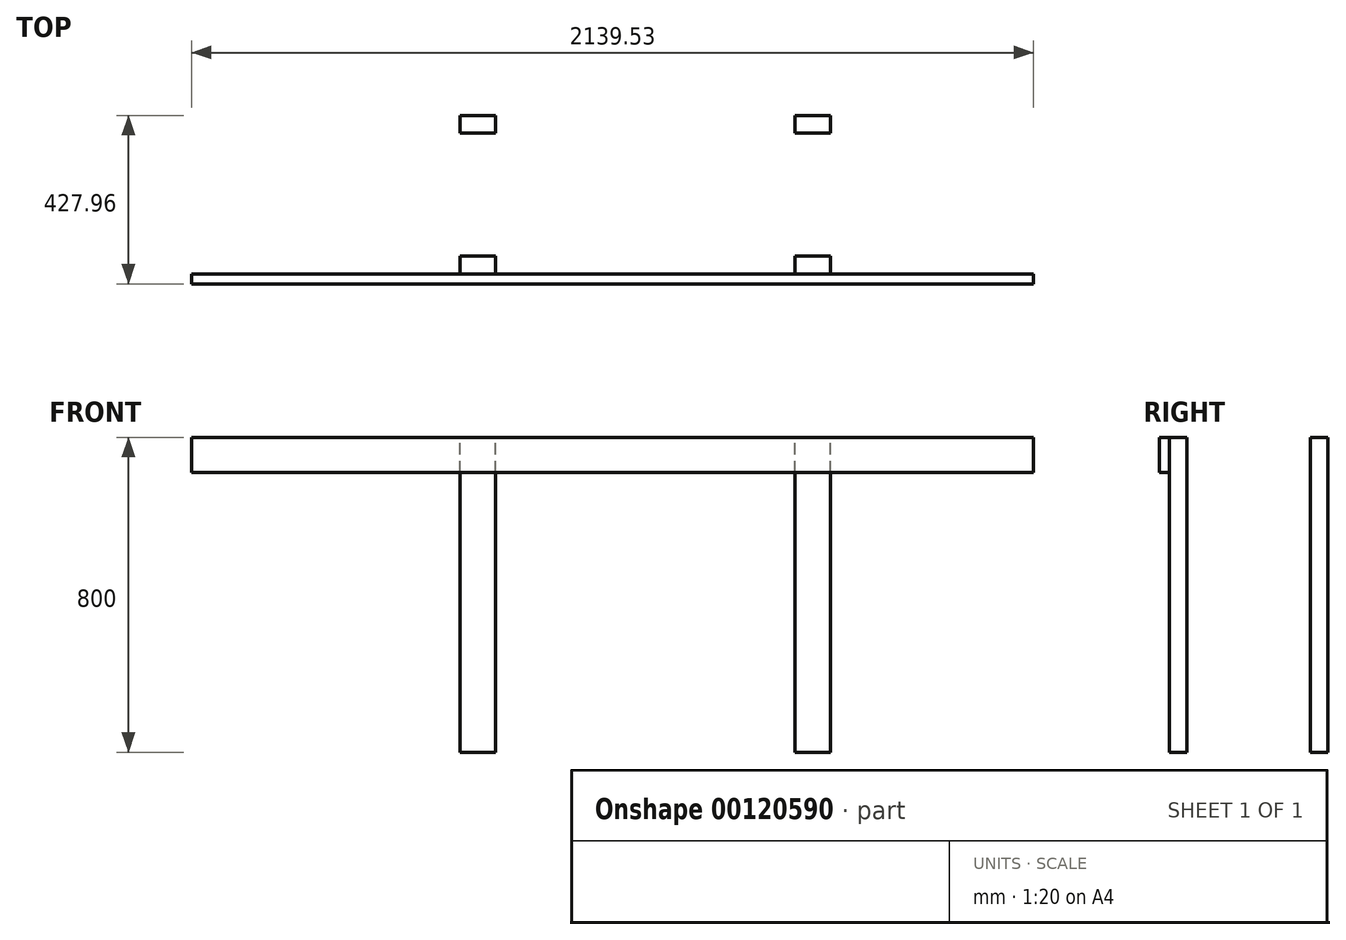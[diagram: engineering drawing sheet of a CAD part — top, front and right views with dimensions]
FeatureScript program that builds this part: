
annotation { "Feature Type Name" : "Feature", "Feature Type Description" : "" }
export const myFeature = defineFeature(function(context is Context, id is Id, definition is map)
    precondition{}
    {
        {
            var Q0;
            Q0=qCreatedBy(makeId("Top.planeOp"),FACE);
            var sketch = newSketch(context, id + "F0", { "sketchPlane" : qUnion([Q0])});
            skLineSegment(sketch, "E0", {"start": v(0, 886.7) * mm, "end": v(0, -768.07) * mm, "construction": true});
            skLineSegment(sketch, "E1", {"start": v(-826.36, 0) * mm, "end": v(826.36, 0) * mm, "construction": true});
            skLineSegment(sketch, "E2.bottom", {"start": v(-1200, 600) * mm, "end": v(1200, 600) * mm});
            skLineSegment(sketch, "E2.top", {"start": v(-1200, -600) * mm, "end": v(1200, -600) * mm});
            skLineSegment(sketch, "E2.left", {"start": v(-1200, 600) * mm, "end": v(-1200, -600) * mm});
            skLineSegment(sketch, "E2.right", {"start": v(1200, 600) * mm, "end": v(1200, -600) * mm});
            skLineSegment(sketch, "E3.bottom", {"start": v(-470.45, 201.48) * mm, "end": v(-380.45, 201.48) * mm});
            skLineSegment(sketch, "E3.top", {"start": v(-470.45, 156.48) * mm, "end": v(-380.45, 156.48) * mm});
            skLineSegment(sketch, "E3.left", {"start": v(-470.45, 201.48) * mm, "end": v(-470.45, 156.48) * mm});
            skLineSegment(sketch, "E3.right", {"start": v(-380.45, 201.48) * mm, "end": v(-380.45, 156.48) * mm});
            skLineSegment(sketch, "E4.MirrorCS", {"start": v(380.45, 201.48) * mm, "end": v(380.45, 156.48) * mm});
            skLineSegment(sketch, "E5.MirrorCS", {"start": v(470.45, 201.48) * mm, "end": v(470.45, 156.48) * mm});
            skLineSegment(sketch, "E6.MirrorCS", {"start": v(470.45, 201.48) * mm, "end": v(380.45, 201.48) * mm});
            skLineSegment(sketch, "E7.MirrorCS", {"start": v(470.45, 156.48) * mm, "end": v(380.45, 156.48) * mm});
            skLineSegment(sketch, "E8.MirrorCS", {"start": v(826.36, 0) * mm, "end": v(-826.36, 0) * mm, "construction": true});
            skLineSegment(sketch, "E9.MirrorCS", {"start": v(-470.45, -156.48) * mm, "end": v(-380.45, -156.48) * mm});
            skLineSegment(sketch, "E10.MirrorCS", {"start": v(-470.45, -201.48) * mm, "end": v(-470.45, -156.48) * mm});
            skLineSegment(sketch, "E11.MirrorCS", {"start": v(-470.45, -201.48) * mm, "end": v(-380.45, -201.48) * mm});
            skLineSegment(sketch, "E12.MirrorCS", {"start": v(-380.45, -201.48) * mm, "end": v(-380.45, -156.48) * mm});
            skLineSegment(sketch, "E13.MirrorCS", {"start": v(470.45, -201.48) * mm, "end": v(470.45, -156.48) * mm});
            skLineSegment(sketch, "E14.MirrorCS", {"start": v(380.45, -201.48) * mm, "end": v(380.45, -156.48) * mm});
            skLineSegment(sketch, "E15.MirrorCS", {"start": v(470.45, -201.48) * mm, "end": v(380.45, -201.48) * mm});
            skLineSegment(sketch, "E16.MirrorCS", {"start": v(470.45, -156.48) * mm, "end": v(380.45, -156.48) * mm});
            skSolve(sketch);
        }
        {
            var Q0;
            Q0=qCreatedBy(makeId("Top.planeOp"),FACE);
            var sketch = newSketch(context, id + "F1", { "sketchPlane" : qUnion([Q0])});
            skLineSegment(sketch, "E17.0.0", {"start": v(-380.45, 201.48) * mm, "end": v(-470.45, 201.48) * mm});
            skLineSegment(sketch, "E17.0.1", {"start": v(-470.45, 201.48) * mm, "end": v(-470.45, 156.48) * mm});
            skLineSegment(sketch, "E17.0.2", {"start": v(-470.45, 156.48) * mm, "end": v(-380.45, 156.48) * mm});
            skLineSegment(sketch, "E17.0.3", {"start": v(-380.45, 156.48) * mm, "end": v(-380.45, 201.48) * mm});
            skLineSegment(sketch, "E17.1.0", {"start": v(-380.45, -156.48) * mm, "end": v(-470.45, -156.48) * mm});
            skLineSegment(sketch, "E17.1.1", {"start": v(-470.45, -156.48) * mm, "end": v(-470.45, -201.48) * mm});
            skLineSegment(sketch, "E17.1.2", {"start": v(-470.45, -201.48) * mm, "end": v(-380.45, -201.48) * mm});
            skLineSegment(sketch, "E17.1.3", {"start": v(-380.45, -201.48) * mm, "end": v(-380.45, -156.48) * mm});
            skLineSegment(sketch, "E17.2.0", {"start": v(470.45, 201.48) * mm, "end": v(380.45, 201.48) * mm});
            skLineSegment(sketch, "E17.2.1", {"start": v(380.45, 201.48) * mm, "end": v(380.45, 156.48) * mm});
            skLineSegment(sketch, "E17.2.2", {"start": v(380.45, 156.48) * mm, "end": v(470.45, 156.48) * mm});
            skLineSegment(sketch, "E17.2.3", {"start": v(470.45, 156.48) * mm, "end": v(470.45, 201.48) * mm});
            skLineSegment(sketch, "E17.3.0", {"start": v(380.45, -201.48) * mm, "end": v(470.45, -201.48) * mm});
            skLineSegment(sketch, "E17.3.1", {"start": v(470.45, -201.48) * mm, "end": v(470.45, -156.48) * mm});
            skLineSegment(sketch, "E17.3.2", {"start": v(470.45, -156.48) * mm, "end": v(380.45, -156.48) * mm});
            skLineSegment(sketch, "E17.3.3", {"start": v(380.45, -156.48) * mm, "end": v(380.45, -201.48) * mm});
            skSolve(sketch);
        }
        {
            var Q0;
            Q0 = qSketchRegion(id + "F1", true);
            extrude(context, id + "F2", {"entities" : qUnion([Q0]), "oppositeDirection" : true, "depth" : 800 * mm});
        }
        {
            var Q0;
            Q0=makeQuery(id+"F2.opExtrude","SWEPT_FACE",FACE,{"disambiguationData":[OSD([sQuery(id+"F1.wireOp",EDGE,"E17.1.2")])]});
            var sketch = newSketch(context, id + "F3", { "sketchPlane" : qUnion([Q0])});
            skLineSegment(sketch, "E18.bottom", {"start": v(-1152.94, 0) * mm, "end": v(986.59, 0) * mm});
            skLineSegment(sketch, "E18.top", {"start": v(-1152.94, -90) * mm, "end": v(986.59, -90) * mm});
            skLineSegment(sketch, "E18.left", {"start": v(-1152.94, 0) * mm, "end": v(-1152.94, -90) * mm});
            skLineSegment(sketch, "E18.right", {"start": v(986.59, 0) * mm, "end": v(986.59, -90) * mm});
            skSolve(sketch);
        }
        {
            var Q0;
            Q0 = qSketchRegion(id + "F3", true);
            extrude(context, id + "F4", {"entities" : qUnion([Q0]), "depth" : 25 * mm});
        }
    });
